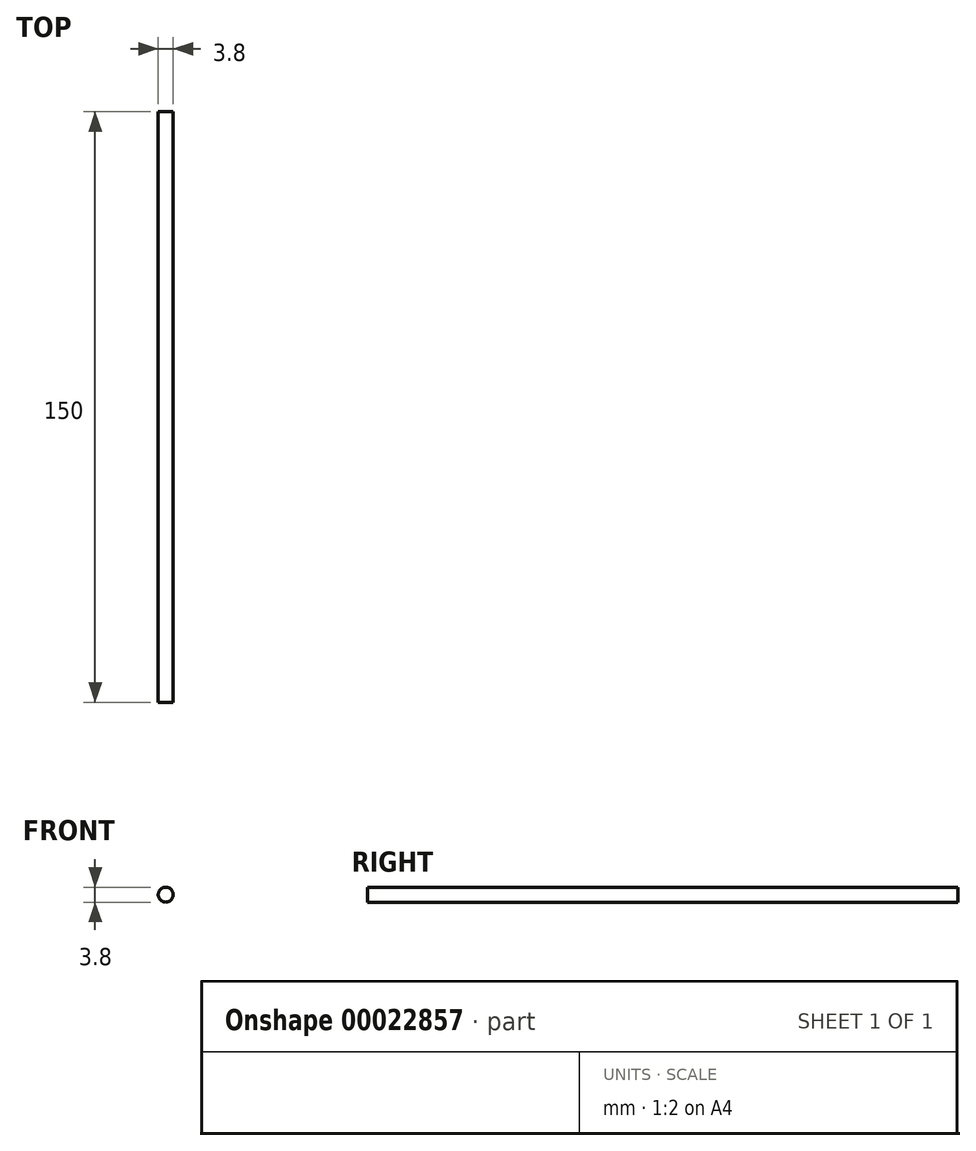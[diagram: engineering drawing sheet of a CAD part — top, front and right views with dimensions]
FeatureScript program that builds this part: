
annotation { "Feature Type Name" : "Feature", "Feature Type Description" : "" }
export const myFeature = defineFeature(function(context is Context, id is Id, definition is map)
    precondition{}
    {
        {
            var Q0;
            Q0=qCreatedBy(makeId("Top.planeOp"),FACE);
            var sketch = newSketch(context, id + "F0", { "sketchPlane" : qUnion([Q0])});
            skLineSegment(sketch, "E0", {"start": v(42.16, 141.07) * mm, "end": v(42.16, -8.93) * mm});
            skLineSegment(sketch, "E1", {"start": v(44.06, 141.07) * mm, "end": v(44.06, 19.15) * mm});
            skLineSegment(sketch, "E2", {"start": v(44.06, 19.15) * mm, "end": v(44.06, -8.93) * mm});
            skLineSegment(sketch, "E3", {"start": v(42.16, 141.07) * mm, "end": v(44.06, 141.07) * mm});
            skLineSegment(sketch, "E4", {"start": v(42.16, 19.15) * mm, "end": v(44.06, 19.15) * mm});
            skLineSegment(sketch, "E5", {"start": v(42.16, -8.93) * mm, "end": v(44.06, -8.93) * mm});
            skSolve(sketch);
        }
        {
            var Q0;
            Q0 = qSketchRegion(id + "F0", true);
            var Q1;
            Q1=sQuery(id+"F0.wireOp",EDGE,"E0");
            revolve(context, id + "F1", {"entities" : qUnion([Q0]), "axis" : qUnion([Q1]), "revolveType" : RevolveType.FULL});
        }
    });
